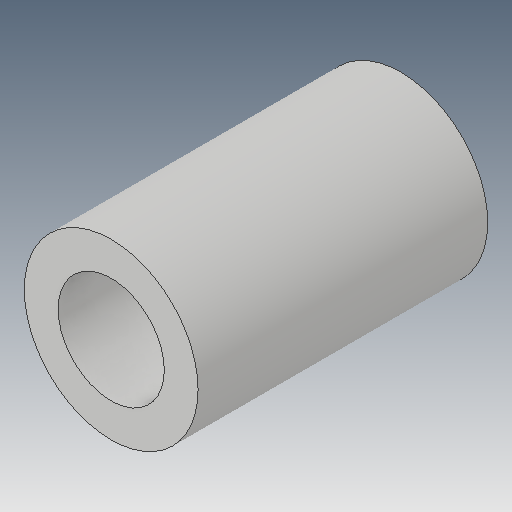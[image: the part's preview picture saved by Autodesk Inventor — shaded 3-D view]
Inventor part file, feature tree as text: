
AUTODESK INVENTOR PART (.ipt)
format: ipt  version: 2017 (Build 210142000, 142)  size: 104,448 bytes
history: native  units: mm
features: other x3, extrude x1, sketch x1, reference x1
ambient origin geometry x8: Origin, YZ Plane, XZ Plane, XY Plane, X Axis, Y Axis, Z Axis, Center Point
bodies: Solid1 (feature_tree)
feature tree (6):
  extrude  "Extrusion1"  Depth=15.0mm
  sketch  "Sketch1"  dims[d0=5.5mm d1=9.0mm d2=15.0mm d3=0.0mm]
  reference  "Reference1"
  other  "Assembly3"
  other  "Delrin Wheel:1"
  other  "SKF 625:1"
